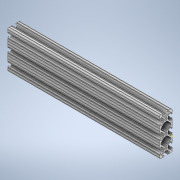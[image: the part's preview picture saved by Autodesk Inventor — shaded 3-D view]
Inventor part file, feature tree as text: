
AUTODESK INVENTOR PART (.ipt)
format: ipt  version: 2020 (Build 240168000, 168)  size: 382,976 bytes
history: native  units: in
note: dims shown in document units (in); Inventor stores cm internally (conversion verified against a paired STEP export)
features: sketch x2, extrude x1
ambient origin geometry x8: Origin, YZ Plane, XZ Plane, XY Plane, X Axis, Y Axis, Z Axis, Center Point
bodies: Solid1 (feature_tree)
feature tree (3):
  extrude  "Extrusion1"  [1 undecoded]
  sketch  "Sketch2"
  sketch  "Sketch1"  dims[d0=12.0in d1=0.0in]
note: 1 required parameter value undecoded (feature->parameter linkage not recoverable at this tier; creation-order binding heuristic only, values carry confidence <= 0.55)
